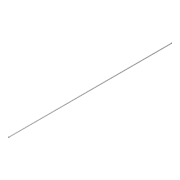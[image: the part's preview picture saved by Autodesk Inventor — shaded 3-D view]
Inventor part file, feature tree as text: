
AUTODESK INVENTOR PART (.ipt)
format: ipt  version: unknown  size: 155,648 bytes
history: native  units: in
note: dims shown in document units (in); Inventor stores cm internally (conversion verified against a paired STEP export)
features: extrude x1, sketch x1
ambient origin geometry x8: Origin, YZ Plane, XZ Plane, XY Plane, X Axis, Y Axis, Z Axis, Center Point
bodies: Solid1 (feature_tree)
feature tree (2):
  extrude  "Extrusion1"  Depth=48.0in TaperAngle=0.0deg
  sketch  "Sketch1"  dims[d0=0.25in d1=48.0in d2=0.0in]
